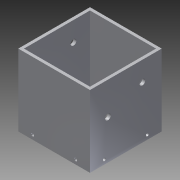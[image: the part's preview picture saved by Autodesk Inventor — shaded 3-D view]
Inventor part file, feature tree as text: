
AUTODESK INVENTOR PART (.ipt)
format: ipt  version: 2013 (Build 170138000, 138)  size: 135,168 bytes
history: native  units: mm
features: sketch x4, hole x3, other x1, extrude x1
ambient origin geometry x1: Origin
feature tree (9):
  other  "ソリッド1"
  extrude  "押し出し1"  Depth=50.0mm
  hole  "穴6"  [1 undecoded]
  hole  "穴16"  [1 undecoded]
  hole  "穴17"  [1 undecoded]
  sketch  "スケッチ1"
  sketch  "スケッチ11"
  sketch  "スケッチ15"
  sketch  "スケッチ16"
note: 3 required parameter values undecoded (feature->parameter linkage not recoverable at this tier; creation-order binding heuristic only, values carry confidence <= 0.55)
